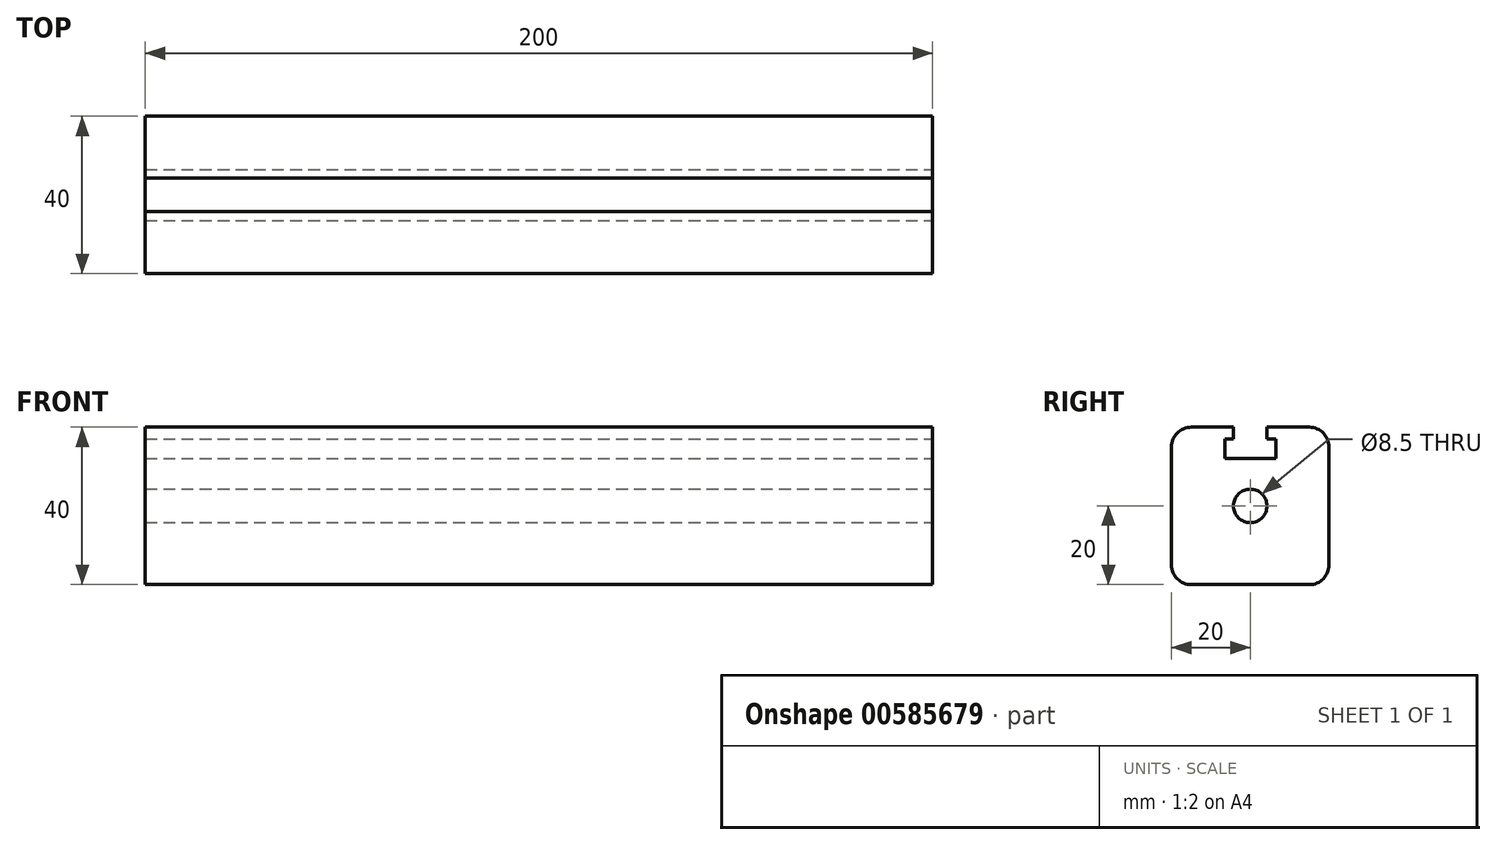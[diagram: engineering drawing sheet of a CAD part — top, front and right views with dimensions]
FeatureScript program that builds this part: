
annotation { "Feature Type Name" : "Feature", "Feature Type Description" : "" }
export const myFeature = defineFeature(function(context is Context, id is Id, definition is map)
    precondition{}
    {
        {
            var Q0;
            Q0=qCreatedBy(makeId("Right.planeOp"),FACE);
            var sketch = newSketch(context, id + "F0", { "sketchPlane" : qUnion([Q0])});
            skLineSegment(sketch, "E0.bottom", {"start": v(-20, -20) * mm, "end": v(20, -20) * mm});
            skLineSegment(sketch, "E0.top", {"start": v(-20, 20) * mm, "end": v(20, 20) * mm});
            skLineSegment(sketch, "E0.left", {"start": v(-20, -20) * mm, "end": v(-20, 20) * mm});
            skLineSegment(sketch, "E0.right", {"start": v(20, -20) * mm, "end": v(20, 20) * mm});
            skPoint(sketch, "E1", {"position": v(-20, 0) * mm});
            skPoint(sketch, "E2", {"position": v(0, -20) * mm});
            skSolve(sketch);
        }
        {
            var Q0;
            Q0=makeQuery(id+"F0.imprint","IMPRINT",FACE,{"disambiguationData":[TD([[makeQuery(id+"F0.imprint","IMPRINT",EDGE,{"derivedFrom":sQuery(id+"F0.wireOp",EDGE,"E0.bottom")}),1.0]])]});
            extrude(context, id + "F1", {"entities" : qUnion([Q0]), "depth" : 200 * mm, "offsetDistance" : 25 * mm});
        }
        {
            var Q0;
            Q0=makeQuery(id+"F1.opExtrude","CAP_FACE",FACE,{"disambiguationData":[OSD([sQuery(id+"F0.wireOp",EDGE,"E0.bottom"),sQuery(id+"F0.wireOp",EDGE,"E0.top"),sQuery(id+"F0.wireOp",EDGE,"E0.left"),sQuery(id+"F0.wireOp",EDGE,"E0.right")])],"isStart":false});
            var sketch = newSketch(context, id + "F2", { "sketchPlane" : qUnion([Q0])});
            skLineSegment(sketch, "E3", {"start": v(-4.25, 20) * mm, "end": v(-4.25, 17) * mm});
            skLineSegment(sketch, "E4", {"start": v(-4.25, 17) * mm, "end": v(-6.5, 17) * mm});
            skLineSegment(sketch, "E5", {"start": v(-6.5, 17) * mm, "end": v(-6.5, 12) * mm});
            skLineSegment(sketch, "E6", {"start": v(-6.5, 12) * mm, "end": v(6.5, 12) * mm});
            skLineSegment(sketch, "E7", {"start": v(6.5, 12) * mm, "end": v(6.5, 17) * mm});
            skLineSegment(sketch, "E8", {"start": v(6.5, 17) * mm, "end": v(4.25, 17) * mm});
            skLineSegment(sketch, "E9", {"start": v(4.25, 17) * mm, "end": v(4.25, 20) * mm});
            skLineSegment(sketch, "E10", {"start": v(4.25, 20) * mm, "end": v(-4.25, 20) * mm});
            skPoint(sketch, "E11", {"position": v(0, 12) * mm});
            skPoint(sketch, "E12", {"position": v(0, 20) * mm});
            skSolve(sketch);
        }
        {
            var Q0;
            Q0=makeQuery(id+"F2.imprint","IMPRINT",FACE,{"disambiguationData":[TD([[makeQuery(id+"F2.imprint","IMPRINT",EDGE,{"derivedFrom":sQuery(id+"F2.wireOp",EDGE,"E3")}),1.0]])]});
            extrude(context, id + "F3", {"entities" : qUnion([Q0]), "operationType" : NewBodyOperationType.REMOVE, "endBound" : BoundingType.UP_TO_NEXT, "oppositeDirection" : true, "depth" : 25 * mm, "offsetDistance" : 25 * mm});
        }
        {
            var Q0;
            Q0=makeQuery(id+"F1.opExtrude","SWEPT_EDGE",EDGE,{"disambiguationData":[OSD([sQuery(id+"F0.wireOp",EDGE,"E0.top"),sQuery(id+"F0.wireOp",EDGE,"E0.right")])]});
            var Q1;
            Q1=makeQuery(id+"F1.opExtrude","SWEPT_EDGE",EDGE,{"disambiguationData":[OSD([sQuery(id+"F0.wireOp",EDGE,"E0.top"),sQuery(id+"F0.wireOp",EDGE,"E0.left")])]});
            var Q2;
            Q2=makeQuery(id+"F1.opExtrude","SWEPT_EDGE",EDGE,{"disambiguationData":[OSD([sQuery(id+"F0.wireOp",EDGE,"E0.bottom"),sQuery(id+"F0.wireOp",EDGE,"E0.right")])]});
            var Q3;
            Q3=makeQuery(id+"F1.opExtrude","SWEPT_EDGE",EDGE,{"disambiguationData":[OSD([sQuery(id+"F0.wireOp",EDGE,"E0.bottom"),sQuery(id+"F0.wireOp",EDGE,"E0.left")])]});
            fillet(context, id + "F4", {"entities" : qUnion([Q0, Q1, Q2, Q3]), "radius" : 5 * mm, "tangentPropagation" : true, "allowEdgeOverflow" : false});
        }
        {
            var Q0;
            Q0=makeQuery(id+"F1.opExtrude","CAP_FACE",FACE,{"disambiguationData":[OSD([sQuery(id+"F0.wireOp",EDGE,"E0.bottom"),sQuery(id+"F0.wireOp",EDGE,"E0.top"),sQuery(id+"F0.wireOp",EDGE,"E0.left"),sQuery(id+"F0.wireOp",EDGE,"E0.right")])],"isStart":false});
            var sketch = newSketch(context, id + "F5", { "sketchPlane" : qUnion([Q0])});
            skCircle(sketch, "E13", {"center": v(0, 0) * mm, "radius": 4.25 * mm});
            skSolve(sketch);
        }
        {
            var Q0;
            Q0=makeQuery(id+"F5.imprint","IMPRINT",FACE,{"disambiguationData":[TD([[makeQuery(id+"F5.imprint","IMPRINT",EDGE,{"derivedFrom":sQuery(id+"F5.wireOp",EDGE,"E13")}),1.0]])]});
            extrude(context, id + "F6", {"entities" : qUnion([Q0]), "operationType" : NewBodyOperationType.REMOVE, "endBound" : BoundingType.UP_TO_NEXT, "oppositeDirection" : true, "depth" : 25 * mm, "offsetDistance" : 25 * mm});
        }
    });
